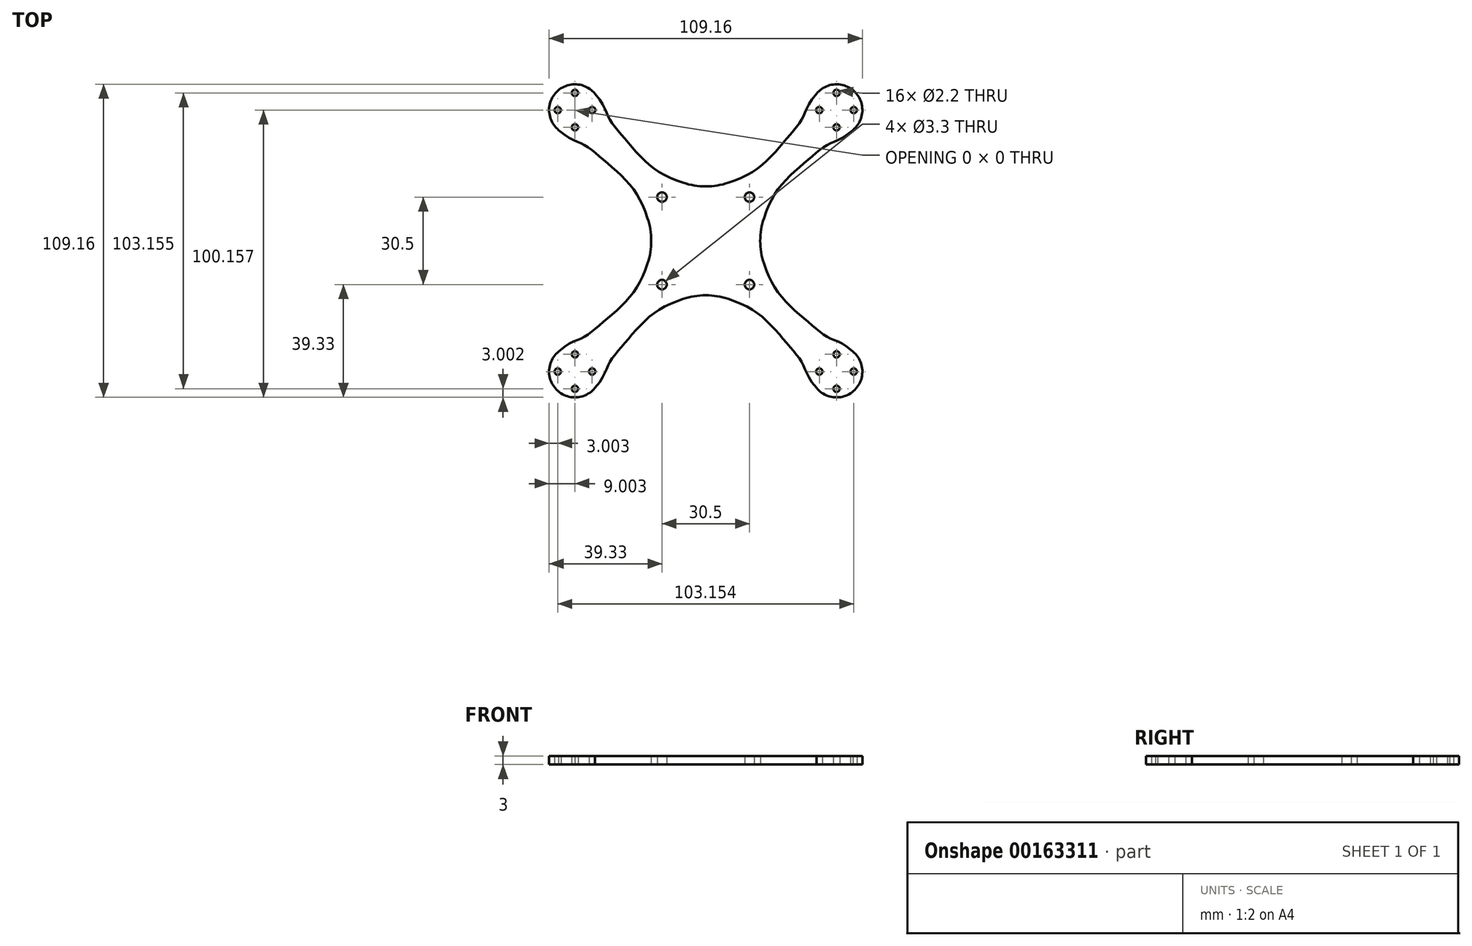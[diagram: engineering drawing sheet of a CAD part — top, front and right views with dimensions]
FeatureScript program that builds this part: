
annotation { "Feature Type Name" : "Feature", "Feature Type Description" : "" }
export const myFeature = defineFeature(function(context is Context, id is Id, definition is map)
    precondition{}
    {
        {
            var Q0;
            Q0=qCreatedBy(makeId("Top.planeOp"),FACE);
            var sketch = newSketch(context, id + "F0", { "sketchPlane" : qUnion([Q0])});
            skCircle(sketch, "E0", {"center": v(-45.58, 45.58) * mm, "radius": 9 * mm});
            skLineSegment(sketch, "E1.bottom", {"start": v(18, 18) * mm, "end": v(-18, 18) * mm});
            skLineSegment(sketch, "E1.top", {"start": v(18, -18) * mm, "end": v(-18, -18) * mm});
            skLineSegment(sketch, "E1.left", {"start": v(18, 18) * mm, "end": v(18, -18) * mm});
            skLineSegment(sketch, "E1.right", {"start": v(-18, 18) * mm, "end": v(-18, -18) * mm});
            skPoint(sketch, "E1.middle", {"position": v(0, 0) * mm});
            skCircle(sketch, "E2", {"center": v(-15.25, 15.25) * mm, "radius": 1.65 * mm});
            skLineSegment(sketch, "E3", {"start": v(0, 75) * mm, "end": v(0, -75) * mm});
            skLineSegment(sketch, "E4", {"start": v(-75, 0) * mm, "end": v(75, 0) * mm});
            skLineSegment(sketch, "E5", {"start": v(75, -75) * mm, "end": v(-75, 75) * mm});
            skCircle(sketch, "E6.MirrorC", {"center": v(15.25, 15.25) * mm, "radius": 1.65 * mm});
            skCircle(sketch, "E7.MirrorC", {"center": v(15.25, -15.25) * mm, "radius": 1.65 * mm});
            skCircle(sketch, "E8.MirrorC", {"center": v(-15.25, -15.25) * mm, "radius": 1.65 * mm});
            skLineSegment(sketch, "E9", {"start": v(-45.58, 45.58) * mm, "end": v(-38.52, 52.6) * mm});
            skLineSegment(sketch, "E10", {"start": v(-45.58, 45.58) * mm, "end": v(-51.96, 39.24) * mm});
            skLineSegment(sketch, "E11", {"start": v(-54.58, 45.58) * mm, "end": v(-36.58, 45.58) * mm});
            skLineSegment(sketch, "E12", {"start": v(-45.58, 36.58) * mm, "end": v(-45.58, 54.58) * mm});
            skCircle(sketch, "E13", {"center": v(-51.58, 45.58) * mm, "radius": 1.1 * mm});
            skCircle(sketch, "E14", {"center": v(-39.58, 45.58) * mm, "radius": 1.1 * mm});
            skCircle(sketch, "E15", {"center": v(-45.58, 51.58) * mm, "radius": 1.1 * mm});
            skCircle(sketch, "E16", {"center": v(-45.58, 39.58) * mm, "radius": 1.1 * mm});
            skFitSpline(sketch, "E17", {"points": [v(-51.96, 39.24) * mm, v(-42.69, 33.65) * mm, v(-35.64, 28.24) * mm, v(-25.31, 18.16) * mm, v(-18, 0) * mm], "startDerivative": vector(58.3, -54.29) * mm, "endDerivative": vector(20.93, -81.1) * mm});
            skFitSpline(sketch, "E18.MirrorCS", {"points": [v(-39.24, 51.96) * mm, v(-33.65, 42.69) * mm, v(-28.24, 35.64) * mm, v(-18.16, 25.31) * mm, v(0, 18) * mm], "startDerivative": vector(54.29, -58.3) * mm, "endDerivative": vector(81.1, -20.93) * mm});
            skFitSpline(sketch, "E19.MirrorCS", {"points": [v(39.24, 51.96) * mm, v(33.65, 42.69) * mm, v(28.24, 35.64) * mm, v(18.16, 25.31) * mm, v(0, 18) * mm], "startDerivative": vector(-54.29, -58.3) * mm, "endDerivative": vector(-81.1, -20.93) * mm});
            skFitSpline(sketch, "E20.MirrorCS", {"points": [v(51.96, 39.24) * mm, v(42.69, 33.65) * mm, v(35.64, 28.24) * mm, v(25.31, 18.16) * mm, v(18, 0) * mm], "startDerivative": vector(-58.3, -54.29) * mm, "endDerivative": vector(-20.93, -81.1) * mm});
            skCircle(sketch, "E21.MirrorC", {"center": v(45.58, 39.58) * mm, "radius": 1.1 * mm});
            skCircle(sketch, "E22.MirrorC", {"center": v(39.58, 45.58) * mm, "radius": 1.1 * mm});
            skCircle(sketch, "E23.MirrorC", {"center": v(45.58, 51.58) * mm, "radius": 1.1 * mm});
            skCircle(sketch, "E24.MirrorC", {"center": v(51.58, 45.58) * mm, "radius": 1.1 * mm});
            skCircle(sketch, "E25.MirrorC", {"center": v(45.58, 45.58) * mm, "radius": 9 * mm});
            skFitSpline(sketch, "E26.MirrorCS", {"points": [v(-51.96, -39.24) * mm, v(-42.69, -33.65) * mm, v(-35.64, -28.24) * mm, v(-25.31, -18.16) * mm, v(-18, 0) * mm], "startDerivative": vector(58.3, 54.29) * mm, "endDerivative": vector(20.93, 81.1) * mm});
            skFitSpline(sketch, "E27.MirrorCS", {"points": [v(-39.24, -51.96) * mm, v(-33.65, -42.69) * mm, v(-28.24, -35.64) * mm, v(-18.16, -25.31) * mm, v(0, -18) * mm], "startDerivative": vector(54.29, 58.3) * mm, "endDerivative": vector(81.1, 20.93) * mm});
            skFitSpline(sketch, "E28.MirrorCS", {"points": [v(39.24, -51.96) * mm, v(33.65, -42.69) * mm, v(28.24, -35.64) * mm, v(18.16, -25.31) * mm, v(0, -18) * mm], "startDerivative": vector(-54.29, 58.3) * mm, "endDerivative": vector(-81.1, 20.93) * mm});
            skFitSpline(sketch, "E29.MirrorCS", {"points": [v(51.96, -39.24) * mm, v(42.69, -33.65) * mm, v(35.64, -28.24) * mm, v(25.31, -18.16) * mm, v(18, 0) * mm], "startDerivative": vector(-58.3, 54.29) * mm, "endDerivative": vector(-20.93, 81.1) * mm});
            skCircle(sketch, "E30.MirrorC", {"center": v(45.58, -45.58) * mm, "radius": 9 * mm});
            skCircle(sketch, "E31.MirrorC", {"center": v(-45.58, -45.58) * mm, "radius": 9 * mm});
            skCircle(sketch, "E32.MirrorC", {"center": v(39.58, -45.58) * mm, "radius": 1.1 * mm});
            skCircle(sketch, "E33.MirrorC", {"center": v(45.58, -51.58) * mm, "radius": 1.1 * mm});
            skCircle(sketch, "E34.MirrorC", {"center": v(51.58, -45.58) * mm, "radius": 1.1 * mm});
            skCircle(sketch, "E35.MirrorC", {"center": v(45.58, -39.58) * mm, "radius": 1.1 * mm});
            skCircle(sketch, "E36.MirrorC", {"center": v(-45.58, -51.58) * mm, "radius": 1.1 * mm});
            skCircle(sketch, "E37.MirrorC", {"center": v(-51.58, -45.58) * mm, "radius": 1.1 * mm});
            skCircle(sketch, "E38.MirrorC", {"center": v(-45.58, -39.58) * mm, "radius": 1.1 * mm});
            skCircle(sketch, "E39.MirrorC", {"center": v(-39.58, -45.58) * mm, "radius": 1.1 * mm});
            skSolve(sketch);
        }
        {
            var Q0;
            Q0 = qSketchRegion(id + "F0", true);
            var Q1;
            {var subQ0=sQuery(id+"F0.wireOp",EDGE,"E11");var subQ1=sQuery(id+"F0.wireOp",EDGE,"E0");var subQ2=makeQuery(id+"F0.imprint","INTERSECT",VERTEX,{"derivedFrom":[subQ1,subQ0]});Q1=makeQuery(id+"F0.imprint","IMPRINT",FACE,{"disambiguationData":[TD([[makeQuery(id+"F0.imprint","IMPRINT",EDGE,{"disambiguationData":[TD([[subQ2,1.0]])],"derivedFrom":subQ1}),1.0]])]});}
            var Q2;
            {var subQ1=sQuery(id+"F0.wireOp",EDGE,"E0");var subQ3=sQuery(id+"F0.wireOp",EDGE,"E12");var subQ7=makeQuery(id+"F0.imprint","INTERSECT",VERTEX,{"disambiguationData":[OD(1.0)],"derivedFrom":[subQ1,subQ3]});Q2=makeQuery(id+"F0.imprint","IMPRINT",FACE,{"disambiguationData":[TD([[makeQuery(id+"F0.imprint","IMPRINT",EDGE,{"disambiguationData":[TD([[subQ7,-1.0]])],"derivedFrom":subQ1}),1.0]])]});}
            var Q3;
            {var subQ0=sQuery(id+"F0.wireOp",EDGE,"E12");var subQ5=sQuery(id+"F0.wireOp",EDGE,"E0");var subQ6=makeQuery(id+"F0.imprint","INTERSECT",VERTEX,{"disambiguationData":[OD(0.0)],"derivedFrom":[subQ5,subQ0]});Q3=makeQuery(id+"F0.imprint","IMPRINT",FACE,{"disambiguationData":[TD([[makeQuery(id+"F0.imprint","IMPRINT",EDGE,{"disambiguationData":[TD([[subQ6,-1.0]])],"derivedFrom":subQ5}),1.0]])]});}
            var Q4;
            {var subQ0=sQuery(id+"F0.wireOp",EDGE,"E11");var subQ1=sQuery(id+"F0.wireOp",EDGE,"E0");var subQ2=makeQuery(id+"F0.imprint","INTERSECT",VERTEX,{"disambiguationData":[OD(1.0)],"derivedFrom":[subQ1,subQ0]});Q4=makeQuery(id+"F0.imprint","IMPRINT",FACE,{"disambiguationData":[TD([[makeQuery(id+"F0.imprint","IMPRINT",EDGE,{"disambiguationData":[TD([[subQ2,1.0]])],"derivedFrom":subQ1}),1.0]])]});}
            extrude(context, id + "F1", {"entities" : qUnion([Q0, Q1, Q2, Q3, Q4]), "depth" : 3 * mm});
        }
        {
            var Q0;
            Q0=makeQuery(id+"F1.opExtrude","SWEPT_EDGE",EDGE,{"disambiguationData":[OSD([sQuery(id+"F0.wireOp",EDGE,"E1.top"),sQuery(id+"F0.wireOp",EDGE,"E3"),sQuery(id+"F0.wireOp",EDGE,"E27.MirrorCS"),sQuery(id+"F0.wireOp",EDGE,"E28.MirrorCS")])]});
            var Q1;
            Q1=makeQuery(id+"F1.opExtrude","SWEPT_EDGE",EDGE,{"disambiguationData":[OSD([sQuery(id+"F0.wireOp",EDGE,"E1.left"),sQuery(id+"F0.wireOp",EDGE,"E4"),sQuery(id+"F0.wireOp",EDGE,"E20.MirrorCS"),sQuery(id+"F0.wireOp",EDGE,"E29.MirrorCS")])]});
            var Q2;
            Q2=makeQuery(id+"F1.opExtrude","SWEPT_EDGE",EDGE,{"disambiguationData":[OSD([sQuery(id+"F0.wireOp",EDGE,"E1.bottom"),sQuery(id+"F0.wireOp",EDGE,"E3"),sQuery(id+"F0.wireOp",EDGE,"E18.MirrorCS"),sQuery(id+"F0.wireOp",EDGE,"E19.MirrorCS")])]});
            var Q3;
            Q3=makeQuery(id+"F1.opExtrude","SWEPT_EDGE",EDGE,{"disambiguationData":[OSD([sQuery(id+"F0.wireOp",EDGE,"E1.right"),sQuery(id+"F0.wireOp",EDGE,"E4"),sQuery(id+"F0.wireOp",EDGE,"E17"),sQuery(id+"F0.wireOp",EDGE,"E26.MirrorCS")])]});
            fillet(context, id + "F2", {"entities" : qUnion([Q0, Q1, Q2, Q3]), "radius" : 25 * mm, "tangentPropagation" : true, "allowEdgeOverflow" : false});
        }
    });
